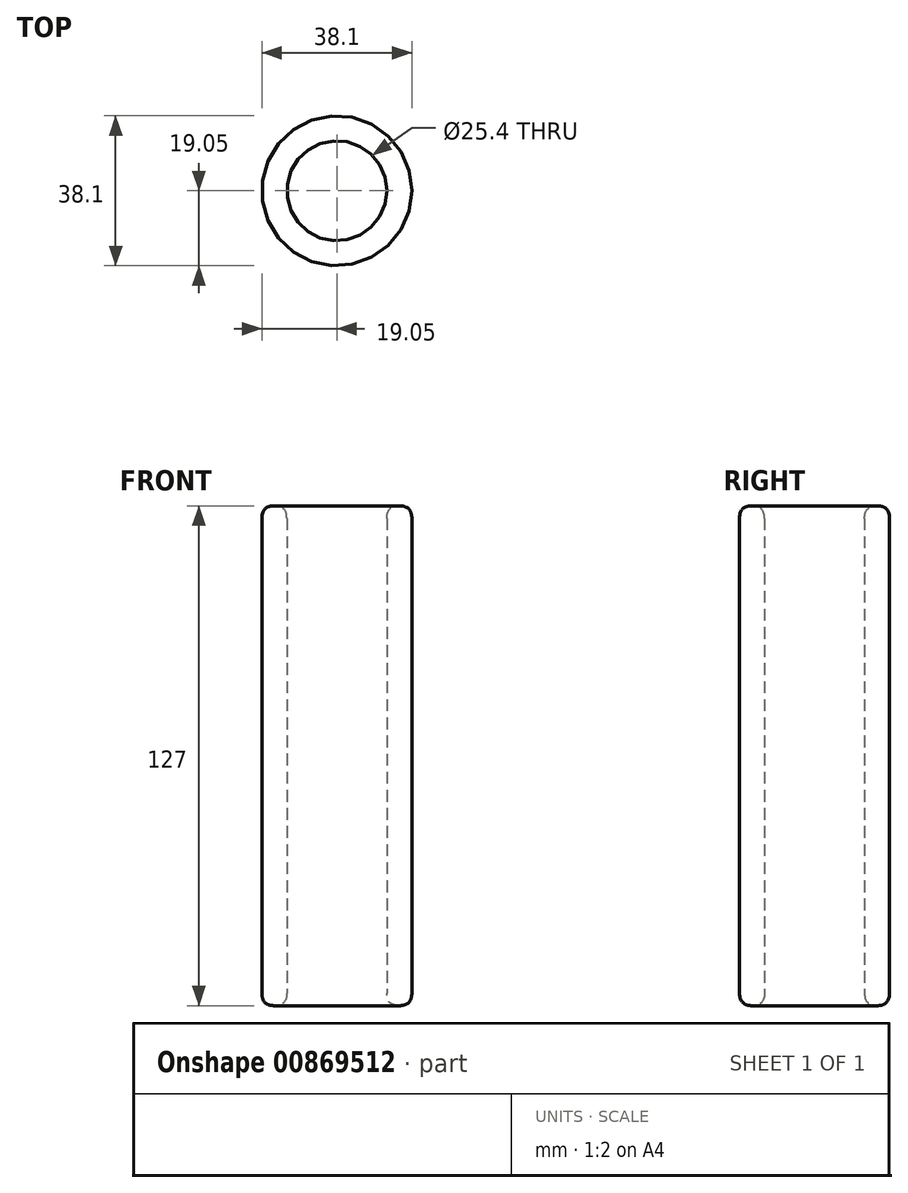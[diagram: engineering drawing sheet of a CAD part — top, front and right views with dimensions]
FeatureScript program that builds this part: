
annotation { "Feature Type Name" : "Feature", "Feature Type Description" : "" }
export const myFeature = defineFeature(function(context is Context, id is Id, definition is map)
    precondition{}
    {
        {
            var Q0;
            Q0=qCreatedBy(makeId("Top.planeOp"),FACE);
            var sketch = newSketch(context, id + "F0", { "sketchPlane" : qUnion([Q0])});
            skCircle(sketch, "E0", {"center": v(0, 0) * mm, "radius": 12.7 * mm});
            skCircle(sketch, "E1.0", {"center": v(0, 0) * mm, "radius": 19.05 * mm});
            skLineSegment(sketch, "E2", {"start": v(0, -19.05) * mm, "end": v(0, 19.05) * mm});
            skSolve(sketch);
        }
        {
            var Q0;
            Q0 = qSketchRegion(id + "F0", true);
            var Q1;
            Q1=sQuery(id+"F0.wireOp",EDGE,"E1.0");
            var Q2;
            Q2=sQuery(id+"F0.wireOp",EDGE,"E0");
            extrude(context, id + "F1", {"entities" : qUnion([Q0]), "surfaceEntities" : qUnion([Q1, Q2]), "depth" : 127 * mm, "offsetDistance" : 25.4 * mm});
        }
        {
            var Q0;
            Q0=makeQuery(id+"F1.opExtrude","CAP_EDGE",EDGE,{"disambiguationData":[OSD([sQuery(id+"F0.wireOp",EDGE,"E0")])],"isStart":false});
            var Q1;
            Q1=makeQuery(id+"F1.opExtrude","CAP_EDGE",EDGE,{"disambiguationData":[OSD([sQuery(id+"F0.wireOp",EDGE,"E1.0")])],"isStart":false});
            var Q2;
            Q2=makeQuery(id+"F1.opExtrude","CAP_EDGE",EDGE,{"disambiguationData":[OSD([sQuery(id+"F0.wireOp",EDGE,"E0")])],"isStart":true});
            var Q3;
            Q3=makeQuery(id+"F1.opExtrude","CAP_EDGE",EDGE,{"disambiguationData":[OSD([sQuery(id+"F0.wireOp",EDGE,"E1.0")])],"isStart":true});
            fillet(context, id + "F2", {"entities" : qUnion([Q0, Q1, Q2, Q3]), "radius" : 3.17 * mm, "tangentPropagation" : true, "rho" : 0.5, "crossSection" : FilletCrossSection.CONIC, "allowEdgeOverflow" : false});
        }
    });
